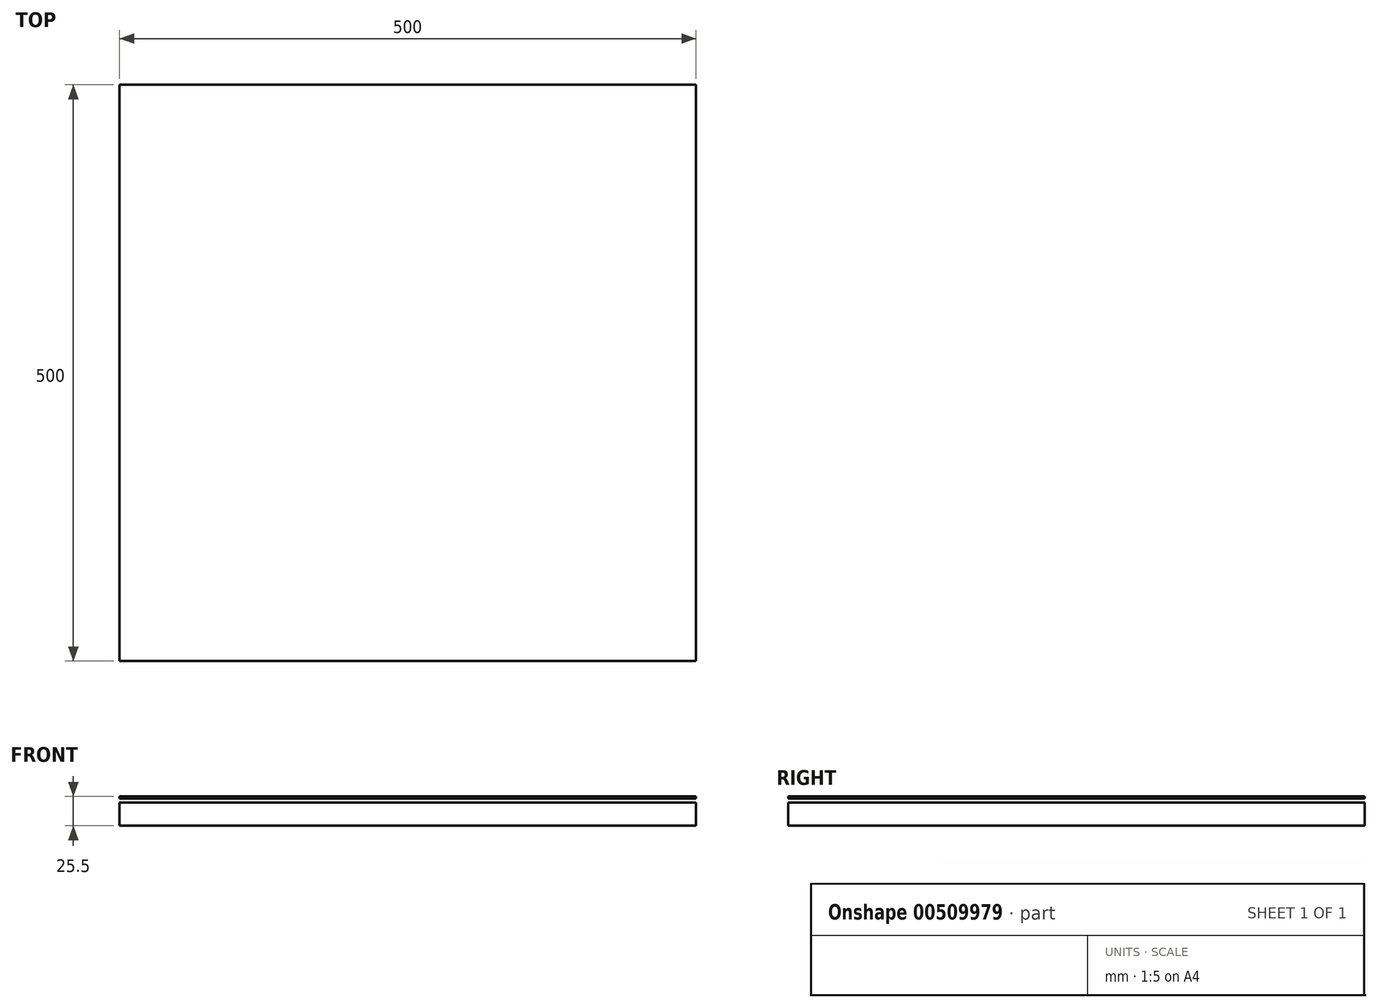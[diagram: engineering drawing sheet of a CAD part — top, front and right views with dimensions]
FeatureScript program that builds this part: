
annotation { "Feature Type Name" : "Feature", "Feature Type Description" : "" }
export const myFeature = defineFeature(function(context is Context, id is Id, definition is map)
    precondition{}
    {
        {
            var Q0;
            Q0=qCreatedBy(makeId("Front.planeOp"),FACE);
            var sketch = newSketch(context, id + "F0", { "sketchPlane" : qUnion([Q0])});
            skLineSegment(sketch, "E0.bottom", {"start": v(0, 0) * mm, "end": v(500, 0) * mm});
            skLineSegment(sketch, "E0.top", {"start": v(0, 20) * mm, "end": v(500, 20) * mm});
            skLineSegment(sketch, "E0.left", {"start": v(0, 0) * mm, "end": v(0, 20) * mm});
            skLineSegment(sketch, "E0.right", {"start": v(500, 0) * mm, "end": v(500, 20) * mm});
            skSolve(sketch);
        }
        {
            var Q0;
            Q0=makeQuery(id+"F0.imprint","IMPRINT",FACE,{"disambiguationData":[TD([[makeQuery(id+"F0.imprint","IMPRINT",EDGE,{"derivedFrom":sQuery(id+"F0.wireOp",EDGE,"E0.bottom")}),1.0]])]});
            var Q1;
            Q1 = qSketchRegion(id + "F0", true);
            extrude(context, id + "F1", {"entities" : qUnion([Q0, Q1]), "endBound" : BoundingType.SYMMETRIC, "depth" : 500 * mm});
        }
        {
            var Q0;
            Q0=qCreatedBy(makeId("Front.planeOp"),FACE);
            var sketch = newSketch(context, id + "F2", { "sketchPlane" : qUnion([Q0])});
            skArc(sketch, "E1", {"start": v(487.5, 20) * mm, "mid": v(484.97, 22.5) * mm, "end": v(482.5, 19.94) * mm});
            skPoint(sketch, "E2", {"position": v(250, 20.13) * mm});
            skLineSegment(sketch, "E3", {"start": v(250, 20.13) * mm, "end": v(250, 5.88) * mm});
            skSolve(sketch);
        }
        {
            var Q0;
            Q0=sQuery(id+"F2.wireOp",EDGE,"E1");
            var Q1;
            Q1=sQuery(id+"F2.wireOp",EDGE,"E3");
            revolve(context, id + "F3", {"bodyType" : ToolBodyType.SURFACE, "surfaceEntities" : qUnion([Q0]), "axis" : qUnion([Q1]), "revolveType" : RevolveType.FULL});
        }
        {
            var Q0;
            Q0=qCreatedBy(makeId("Front.planeOp"),FACE);
            var sketch = newSketch(context, id + "F4", { "sketchPlane" : qUnion([Q0])});
            skLineSegment(sketch, "E4", {"start": v(482.45, 19.96) * mm, "end": v(482.45, 23.46) * mm});
            skLineSegment(sketch, "E5", {"start": v(487.47, 19.96) * mm, "end": v(487.47, 23.46) * mm});
            skLineSegment(sketch, "E6", {"start": v(482.45, 23.46) * mm, "end": v(487.47, 23.46) * mm});
            skSolve(sketch);
        }
        {
            var Q0;
            Q0=sQuery(id+"F4.wireOp",EDGE,"E6");
            var Q1;
            Q1=sQuery(id+"F4.wireOp",EDGE,"E5");
            var Q2;
            Q2=sQuery(id+"F4.wireOp",EDGE,"E4");
            var Q3;
            Q3=sQuery(id+"F2.wireOp",EDGE,"E3");
            revolve(context, id + "F5", {"bodyType" : ToolBodyType.SURFACE, "surfaceEntities" : qUnion([Q0, Q1, Q2]), "axis" : qUnion([Q3]), "revolveType" : RevolveType.FULL});
        }
        {
            var Q0;
            Q0=qCreatedBy(makeId("Front.planeOp"),FACE);
            var sketch = newSketch(context, id + "F6", { "sketchPlane" : qUnion([Q0])});
            skLineSegment(sketch, "E7.bottom", {"start": v(0, 23.5) * mm, "end": v(500, 23.5) * mm});
            skLineSegment(sketch, "E7.top", {"start": v(0, 25.5) * mm, "end": v(500, 25.5) * mm});
            skLineSegment(sketch, "E7.left", {"start": v(0, 23.5) * mm, "end": v(0, 25.5) * mm});
            skLineSegment(sketch, "E7.right", {"start": v(500, 23.5) * mm, "end": v(500, 25.5) * mm});
            skSolve(sketch);
        }
        {
            var Q0;
            Q0 = qSketchRegion(id + "F6", true);
            extrude(context, id + "F7", {"entities" : qUnion([Q0]), "endBound" : BoundingType.SYMMETRIC, "depth" : 500 * mm});
        }
        {
            var Q0;
            Q0=qCreatedBy(makeId("Front.planeOp"),FACE);
            var sketch = newSketch(context, id + "F8", { "sketchPlane" : qUnion([Q0])});
            skLineSegment(sketch, "E8", {"start": v(329.83, 25.51) * mm, "end": v(329.83, 29.01) * mm});
            skLineSegment(sketch, "E9", {"start": v(329.83, 29.01) * mm, "end": v(334.83, 29.01) * mm});
            skLineSegment(sketch, "E10", {"start": v(334.83, 29.01) * mm, "end": v(334.83, 25.54) * mm});
            skSolve(sketch);
        }
        {
            var Q0;
            Q0=qCreatedBy(makeId("Front.planeOp"),FACE);
            var sketch = newSketch(context, id + "F9", { "sketchPlane" : qUnion([Q0])});
            skArc(sketch, "E11", {"start": v(334.86, 25.46) * mm, "mid": v(332.38, 27.98) * mm, "end": v(329.86, 25.5) * mm});
            skSolve(sketch);
        }
        {
            var Q0;
            Q0=sQuery(id+"F9.wireOp",EDGE,"E11");
            var Q1;
            Q1=sQuery(id+"F2.wireOp",EDGE,"E3");
            revolve(context, id + "F10", {"bodyType" : ToolBodyType.SURFACE, "surfaceEntities" : qUnion([Q0]), "axis" : qUnion([Q1]), "revolveType" : RevolveType.FULL});
        }
        {
            var Q0;
            Q0=sQuery(id+"F8.wireOp",EDGE,"E10");
            var Q1;
            Q1=sQuery(id+"F8.wireOp",EDGE,"E9");
            var Q2;
            Q2=sQuery(id+"F8.wireOp",EDGE,"E8");
            var Q3;
            Q3=sQuery(id+"F2.wireOp",EDGE,"E3");
            revolve(context, id + "F11", {"bodyType" : ToolBodyType.SURFACE, "surfaceEntities" : qUnion([Q0, Q1, Q2]), "axis" : qUnion([Q3]), "revolveType" : RevolveType.FULL});
        }
    });
